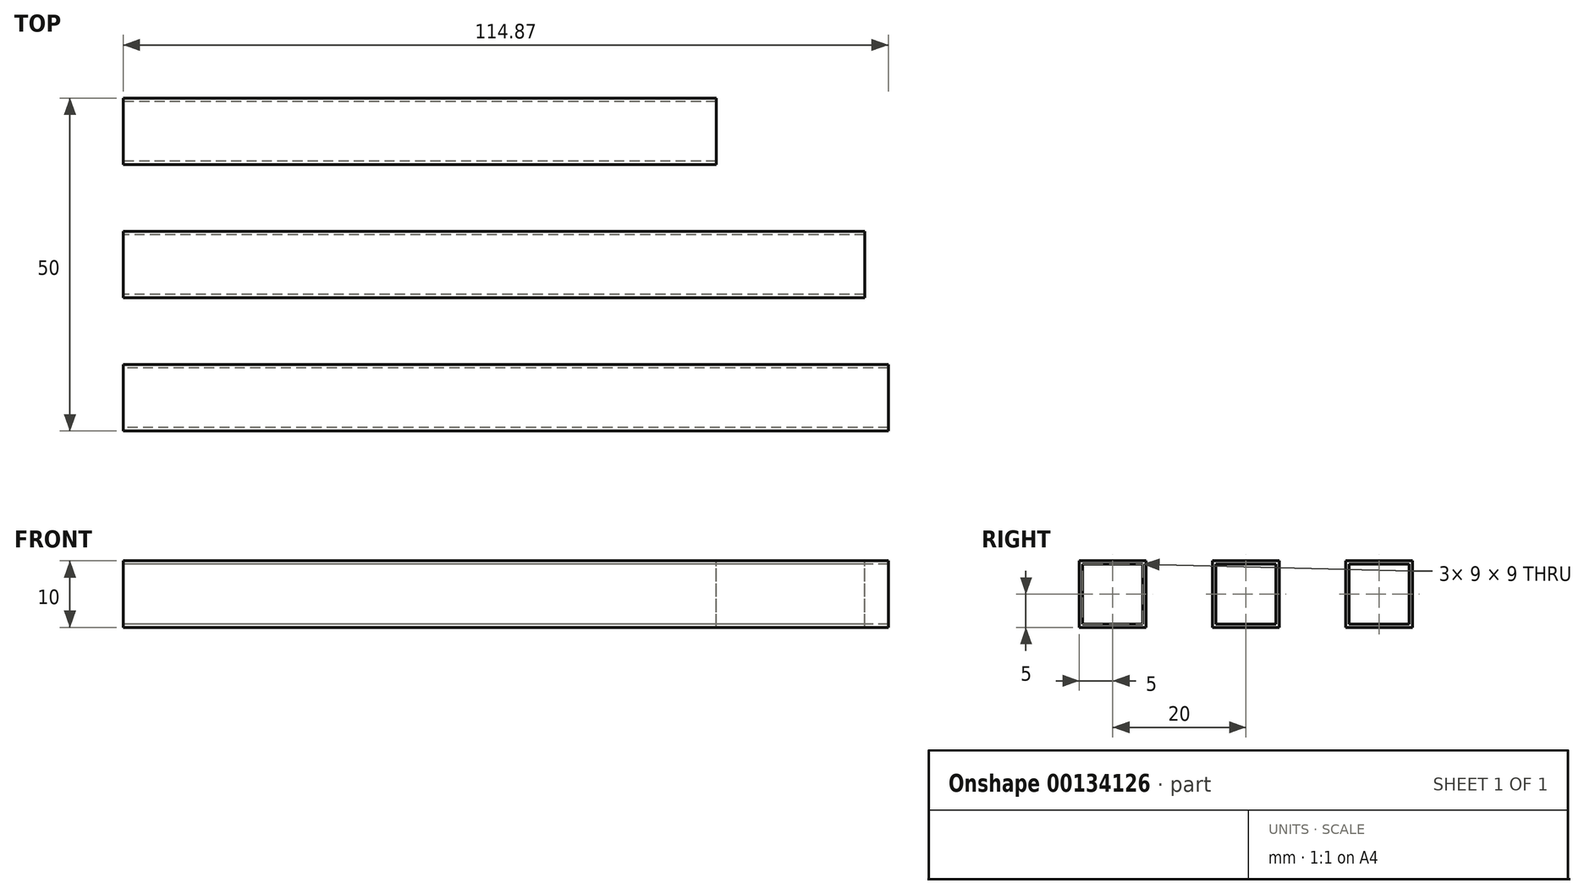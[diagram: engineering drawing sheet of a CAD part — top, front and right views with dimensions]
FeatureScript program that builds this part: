
annotation { "Feature Type Name" : "Feature", "Feature Type Description" : "" }
export const myFeature = defineFeature(function(context is Context, id is Id, definition is map)
    precondition{}
    {
        {
            var Q0;
            Q0=qCreatedBy(makeId("Front.planeOp"),FACE);
            var sketch = newSketch(context, id + "F0", { "sketchPlane" : qUnion([Q0])});
            skLineSegment(sketch, "E0", {"start": v(-75.03, 0) * mm, "end": v(74.55, 0) * mm});
            skSolve(sketch);
        }
        {
            var Q0;
            Q0=qCreatedBy(makeId("Right.planeOp"),FACE);
            var sketch = newSketch(context, id + "F1", { "sketchPlane" : qUnion([Q0])});
            skLineSegment(sketch, "E1.bottom", {"start": v(-5, -5) * mm, "end": v(5, -5) * mm});
            skLineSegment(sketch, "E1.top", {"start": v(-5, 5) * mm, "end": v(5, 5) * mm});
            skLineSegment(sketch, "E1.left", {"start": v(-5, -5) * mm, "end": v(-5, 5) * mm});
            skLineSegment(sketch, "E1.right", {"start": v(5, -5) * mm, "end": v(5, 5) * mm});
            skPoint(sketch, "E1.middle", {"position": v(0, 0) * mm});
            skLineSegment(sketch, "E2.bottom", {"start": v(-4.5, -4.5) * mm, "end": v(4.5, -4.5) * mm});
            skLineSegment(sketch, "E2.top", {"start": v(-4.5, 4.5) * mm, "end": v(4.5, 4.5) * mm});
            skLineSegment(sketch, "E2.left", {"start": v(-4.5, -4.5) * mm, "end": v(-4.5, 4.5) * mm});
            skLineSegment(sketch, "E2.right", {"start": v(4.5, -4.5) * mm, "end": v(4.5, 4.5) * mm});
            skSolve(sketch);
        }
        {
            var Q0;
            Q0=makeQuery(id+"F1.imprint","IMPRINT",FACE,{"disambiguationData":[TD([[makeQuery(id+"F1.imprint","IMPRINT",EDGE,{"derivedFrom":sQuery(id+"F1.wireOp",EDGE,"E1.bottom")}),1.0]])]});
            extrude(context, id + "F2", {"entities" : qUnion([Q0]), "depth" : 89.03 * mm});
        }
        {
            var Q0;
            Q0=qCreatedBy(makeId("Right.planeOp"),FACE);
            var sketch = newSketch(context, id + "F3", { "sketchPlane" : qUnion([Q0])});
            skLineSegment(sketch, "E3.bottom", {"start": v(-25, -5) * mm, "end": v(-15, -5) * mm});
            skLineSegment(sketch, "E3.top", {"start": v(-25, 5) * mm, "end": v(-15, 5) * mm});
            skLineSegment(sketch, "E3.left", {"start": v(-25, -5) * mm, "end": v(-25, 5) * mm});
            skLineSegment(sketch, "E3.right", {"start": v(-15, -5) * mm, "end": v(-15, 5) * mm});
            skPoint(sketch, "E3.middle", {"position": v(-20, 0) * mm});
            skLineSegment(sketch, "E4.bottom", {"start": v(-24.5, -4.5) * mm, "end": v(-15.5, -4.5) * mm});
            skLineSegment(sketch, "E4.top", {"start": v(-24.5, 4.5) * mm, "end": v(-15.5, 4.5) * mm});
            skLineSegment(sketch, "E4.left", {"start": v(-24.5, -4.5) * mm, "end": v(-24.5, 4.5) * mm});
            skLineSegment(sketch, "E4.right", {"start": v(-15.5, -4.5) * mm, "end": v(-15.5, 4.5) * mm});
            skSolve(sketch);
        }
        {
            var Q0;
            Q0=makeQuery(id+"F3.imprint","IMPRINT",FACE,{"disambiguationData":[TD([[makeQuery(id+"F3.imprint","IMPRINT",EDGE,{"derivedFrom":sQuery(id+"F3.wireOp",EDGE,"E3.bottom")}),1.0]])]});
            extrude(context, id + "F4", {"entities" : qUnion([Q0]), "depth" : 111.31 * mm});
        }
        {
            var Q0;
            Q0=qCreatedBy(makeId("Right.planeOp"),FACE);
            var sketch = newSketch(context, id + "F5", { "sketchPlane" : qUnion([Q0])});
            skLineSegment(sketch, "E5.bottom", {"start": v(-45, -5) * mm, "end": v(-35, -5) * mm});
            skLineSegment(sketch, "E5.top", {"start": v(-45, 5) * mm, "end": v(-35, 5) * mm});
            skLineSegment(sketch, "E5.left", {"start": v(-45, -5) * mm, "end": v(-45, 5) * mm});
            skLineSegment(sketch, "E5.right", {"start": v(-35, -5) * mm, "end": v(-35, 5) * mm});
            skPoint(sketch, "E5.middle", {"position": v(-40, 0) * mm});
            skLineSegment(sketch, "E6.bottom", {"start": v(-44.5, -4.5) * mm, "end": v(-35.5, -4.5) * mm});
            skLineSegment(sketch, "E6.top", {"start": v(-44.5, 4.5) * mm, "end": v(-35.5, 4.5) * mm});
            skLineSegment(sketch, "E6.left", {"start": v(-44.5, -4.5) * mm, "end": v(-44.5, 4.5) * mm});
            skLineSegment(sketch, "E6.right", {"start": v(-35.5, -4.5) * mm, "end": v(-35.5, 4.5) * mm});
            skSolve(sketch);
        }
        {
            var Q0;
            Q0=qSketchRegion(id+"F5",true);
            extrude(context, id + "F6", {"entities" : qUnion([Q0]), "depth" : 114.87 * mm});
        }
        {
            var Q0;
            Q0=makeQuery(id+"F2.opExtrude","CAP_FACE",FACE,{"disambiguationData":[OSD([sQuery(id+"F1.wireOp",EDGE,"E1.bottom"),sQuery(id+"F1.wireOp",EDGE,"E1.top"),sQuery(id+"F1.wireOp",EDGE,"E1.left"),sQuery(id+"F1.wireOp",EDGE,"E1.right"),sQuery(id+"F1.wireOp",EDGE,"E2.bottom"),sQuery(id+"F1.wireOp",EDGE,"E2.top"),sQuery(id+"F1.wireOp",EDGE,"E2.left"),sQuery(id+"F1.wireOp",EDGE,"E2.right")])],"isStart":false});
            var sketch = newSketch(context, id + "F7", { "sketchPlane" : qUnion([Q0])});
            skPoint(sketch, "E7", {"position": v(0, 0) * mm});
            skSolve(sketch);
        }
        {
            var Q0;
            Q0=makeQuery(id+"F4.opExtrude","CAP_FACE",FACE,{"disambiguationData":[OSD([sQuery(id+"F3.wireOp",EDGE,"E3.bottom"),sQuery(id+"F3.wireOp",EDGE,"E3.top"),sQuery(id+"F3.wireOp",EDGE,"E3.left"),sQuery(id+"F3.wireOp",EDGE,"E3.right"),sQuery(id+"F3.wireOp",EDGE,"E4.bottom"),sQuery(id+"F3.wireOp",EDGE,"E4.top"),sQuery(id+"F3.wireOp",EDGE,"E4.left"),sQuery(id+"F3.wireOp",EDGE,"E4.right")])],"isStart":false});
            var sketch = newSketch(context, id + "F8", { "sketchPlane" : qUnion([Q0])});
            skLineSegment(sketch, "E8", {"start": v(-24.5, 4.5) * mm, "end": v(-15.5, -4.5) * mm, "construction": true});
            skLineSegment(sketch, "E9", {"start": v(-15.5, 4.5) * mm, "end": v(-24.5, -4.5) * mm, "construction": true});
            skPoint(sketch, "E10", {"position": v(-20, 0) * mm});
            skSolve(sketch);
        }
        {
            var Q0;
            Q0=makeQuery(id+"F6.opExtrude","CAP_FACE",FACE,{"disambiguationData":[OSD([sQuery(id+"F5.wireOp",EDGE,"E5.bottom"),sQuery(id+"F5.wireOp",EDGE,"E5.top"),sQuery(id+"F5.wireOp",EDGE,"E5.left"),sQuery(id+"F5.wireOp",EDGE,"E5.right"),sQuery(id+"F5.wireOp",EDGE,"E6.bottom"),sQuery(id+"F5.wireOp",EDGE,"E6.top"),sQuery(id+"F5.wireOp",EDGE,"E6.left"),sQuery(id+"F5.wireOp",EDGE,"E6.right")])],"isStart":false});
            var sketch = newSketch(context, id + "F9", { "sketchPlane" : qUnion([Q0])});
            skLineSegment(sketch, "E11", {"start": v(-44.5, 4.5) * mm, "end": v(-35.5, -4.5) * mm, "construction": true});
            skLineSegment(sketch, "E12", {"start": v(-35.5, 4.5) * mm, "end": v(-44.5, -4.5) * mm, "construction": true});
            skPoint(sketch, "E13", {"position": v(-40, 0) * mm});
            skSolve(sketch);
        }
    });
